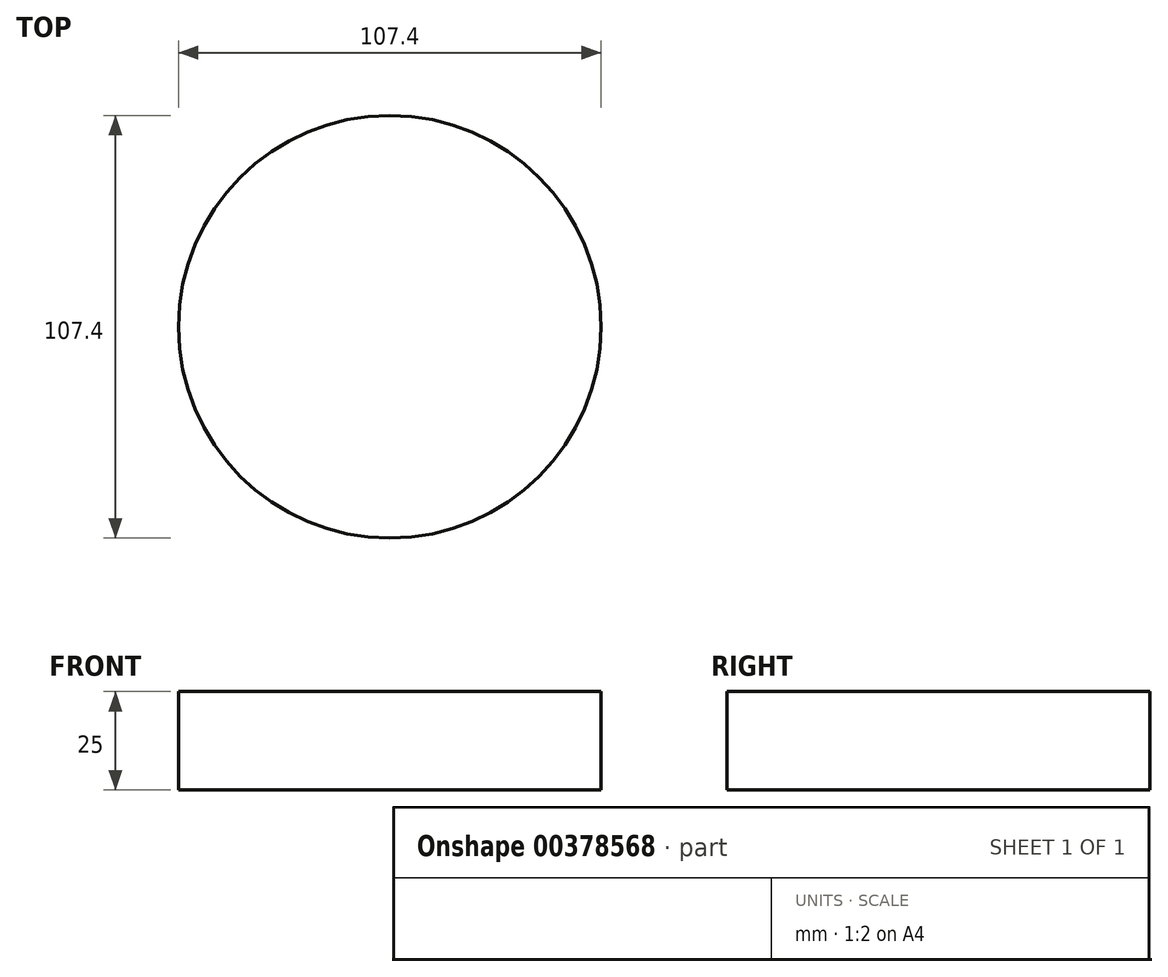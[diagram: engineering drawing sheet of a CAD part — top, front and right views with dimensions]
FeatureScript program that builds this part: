
annotation { "Feature Type Name" : "Feature", "Feature Type Description" : "" }
export const myFeature = defineFeature(function(context is Context, id is Id, definition is map)
    precondition{}
    {
        {
            var Q0;
            Q0=qCreatedBy(makeId("Top.planeOp"),FACE);
            var sketch = newSketch(context, id + "F0", { "sketchPlane" : qUnion([Q0])});
            skCircle(sketch, "E0", {"center": v(0, 0) * mm, "radius": 53.7 * mm});
            skSolve(sketch);
        }
        {
            var Q0;
            Q0=qCreatedBy(makeId("Top.planeOp"),FACE);
            var sketch = newSketch(context, id + "F1", { "sketchPlane" : qUnion([Q0])});
            skCircle(sketch, "E1", {"center": v(0, 0) * mm, "radius": 36.2 * mm});
            skSolve(sketch);
        }
        {
            var Q0;
            Q0=sQuery(id+"F1.wireOp",EDGE,"E1");
            extrude(context, id + "F2", {"bodyType" : ToolBodyType.SURFACE, "surfaceEntities" : qUnion([Q0]), "depth" : 25 * mm});
        }
        {
            var Q0;
            Q0=makeQuery(id+"F0.imprint","IMPRINT",FACE,{"disambiguationData":[TD([[makeQuery(id+"F0.imprint","IMPRINT",EDGE,{"derivedFrom":sQuery(id+"F0.wireOp",EDGE,"E0")}),1.0]])]});
            extrude(context, id + "F3", {"entities" : qUnion([Q0]), "depth" : 25 * mm});
        }
    });
